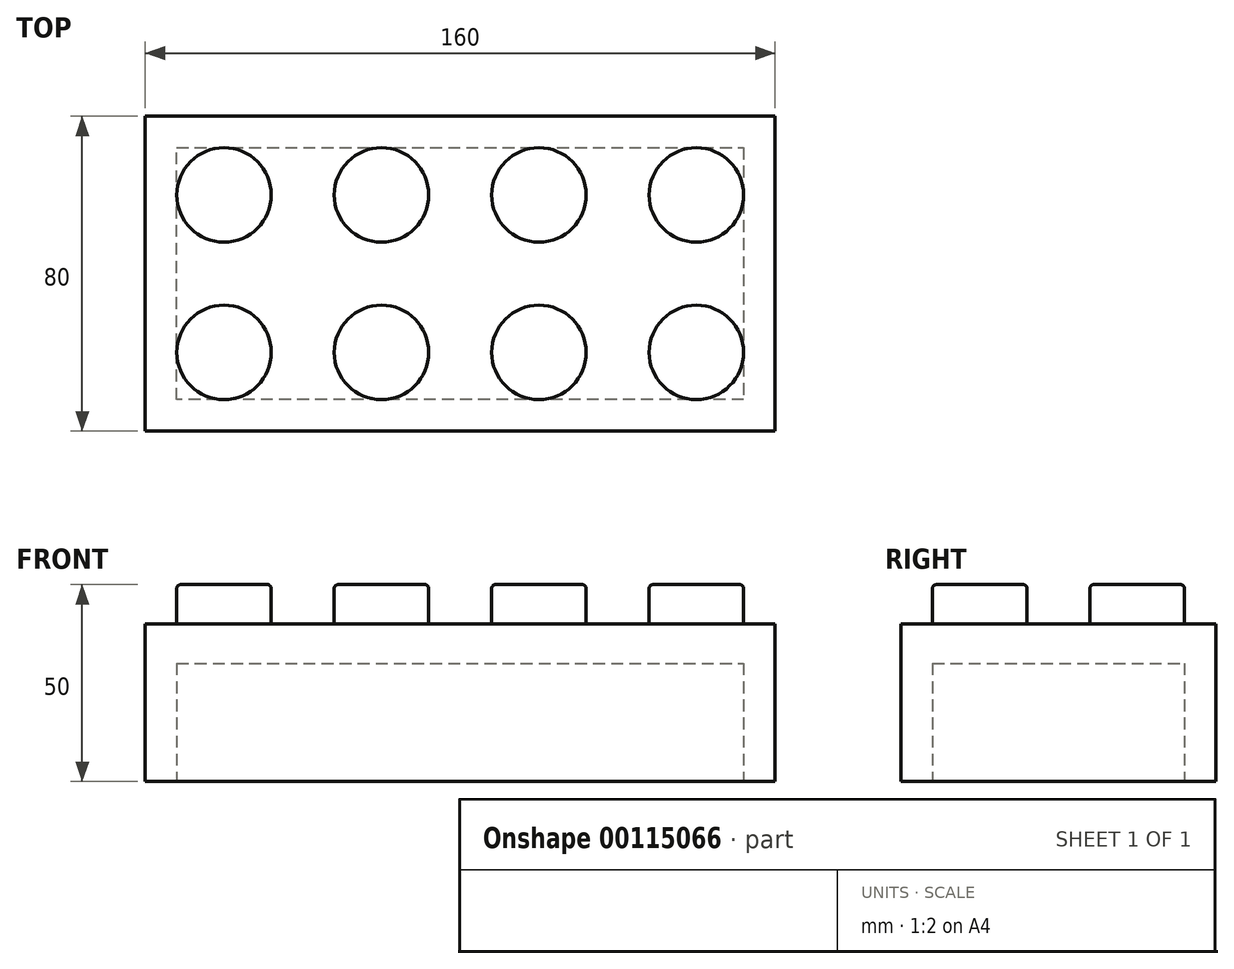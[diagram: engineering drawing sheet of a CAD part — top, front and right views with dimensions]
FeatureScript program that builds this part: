
annotation { "Feature Type Name" : "Feature", "Feature Type Description" : "" }
export const myFeature = defineFeature(function(context is Context, id is Id, definition is map)
    precondition{}
    {
        {
            var Q0;
            Q0=qCreatedBy(makeId("Top.planeOp"),FACE);
            var sketch = newSketch(context, id + "F0", { "sketchPlane" : qUnion([Q0])});
            skLineSegment(sketch, "E0.bottom", {"start": v(-96.29, 42.55) * mm, "end": v(63.71, 42.55) * mm});
            skLineSegment(sketch, "E0.top", {"start": v(-96.29, -37.45) * mm, "end": v(63.71, -37.45) * mm});
            skLineSegment(sketch, "E0.left", {"start": v(-96.29, 42.55) * mm, "end": v(-96.29, -37.45) * mm});
            skLineSegment(sketch, "E0.right", {"start": v(63.71, 42.55) * mm, "end": v(63.71, -37.45) * mm});
            skSolve(sketch);
        }
        {
            var Q0;
            Q0 = qSketchRegion(id + "F0", true);
            extrude(context, id + "F1", {"entities" : qUnion([Q0]), "depth" : 40 * mm});
        }
        {
            var Q0;
            Q0=makeQuery(id+"F1.opExtrude","CAP_FACE",FACE,{"disambiguationData":[OSD([sQuery(id+"F0.wireOp",EDGE,"E0.bottom"),sQuery(id+"F0.wireOp",EDGE,"E0.top"),sQuery(id+"F0.wireOp",EDGE,"E0.left"),sQuery(id+"F0.wireOp",EDGE,"E0.right")])],"isStart":true});
            var sketch = newSketch(context, id + "F2", { "sketchPlane" : qUnion([Q0])});
            skLineSegment(sketch, "E1.0", {"start": v(-88.29, -34.55) * mm, "end": v(55.71, -34.55) * mm});
            skLineSegment(sketch, "E1.1", {"start": v(-88.29, 29.45) * mm, "end": v(-88.29, -34.55) * mm});
            skLineSegment(sketch, "E1.2", {"start": v(55.71, 29.45) * mm, "end": v(-88.29, 29.45) * mm});
            skLineSegment(sketch, "E1.3", {"start": v(55.71, -34.55) * mm, "end": v(55.71, 29.45) * mm});
            skSolve(sketch);
        }
        {
            var Q0;
            Q0 = qSketchRegion(id + "F2", true);
            extrude(context, id + "F3", {"entities" : qUnion([Q0]), "operationType" : NewBodyOperationType.REMOVE, "oppositeDirection" : true, "depth" : 30 * mm});
        }
        {
            var Q0;
            Q0=makeQuery(id+"F1.opExtrude","CAP_FACE",FACE,{"disambiguationData":[OSD([sQuery(id+"F0.wireOp",EDGE,"E0.bottom"),sQuery(id+"F0.wireOp",EDGE,"E0.top"),sQuery(id+"F0.wireOp",EDGE,"E0.left"),sQuery(id+"F0.wireOp",EDGE,"E0.right")])],"isStart":false});
            var sketch = newSketch(context, id + "F4", { "sketchPlane" : qUnion([Q0])});
            skCircle(sketch, "E2", {"center": v(-76.29, 22.55) * mm, "radius": 12 * mm});
            skCircle(sketch, "E3.0.1.0", {"center": v(-76.29, -17.45) * mm, "radius": 12 * mm});
            skCircle(sketch, "E3.1.0.0", {"center": v(-36.29, 22.55) * mm, "radius": 12 * mm});
            skCircle(sketch, "E3.1.1.0", {"center": v(-36.29, -17.45) * mm, "radius": 12 * mm});
            skCircle(sketch, "E3.2.0.0", {"center": v(3.71, 22.55) * mm, "radius": 12 * mm});
            skCircle(sketch, "E3.2.1.0", {"center": v(3.71, -17.45) * mm, "radius": 12 * mm});
            skCircle(sketch, "E3.3.0.0", {"center": v(43.71, 22.55) * mm, "radius": 12 * mm});
            skCircle(sketch, "E3.3.1.0", {"center": v(43.71, -17.45) * mm, "radius": 12 * mm});
            skLineSegment(sketch, "E3.direction1", {"start": v(-76.29, 22.55) * mm, "end": v(-36.29, 22.55) * mm, "construction": true});
            skLineSegment(sketch, "E3.direction2", {"start": v(-76.29, 22.55) * mm, "end": v(-76.29, -17.45) * mm, "construction": true});
            skSolve(sketch);
        }
        {
            var Q0;
            Q0 = qSketchRegion(id + "F4", true);
            extrude(context, id + "F5", {"entities" : qUnion([Q0]), "operationType" : NewBodyOperationType.ADD, "depth" : 10 * mm});
        }
        {
            var Q0;
            Q0=makeQuery(id+"F5.opExtrude","CAP_FACE",FACE,{"disambiguationData":[OSD([sQuery(id+"F4.wireOp",EDGE,"E2")])],"isStart":false});
            var Q1;
            Q1=makeQuery(id+"F5.opExtrude","CAP_FACE",FACE,{"disambiguationData":[OSD([sQuery(id+"F4.wireOp",EDGE,"E3.1.0.0")])],"isStart":false});
            var Q2;
            Q2=makeQuery(id+"F5.opExtrude","CAP_FACE",FACE,{"disambiguationData":[OSD([sQuery(id+"F4.wireOp",EDGE,"E3.2.0.0")])],"isStart":false});
            var Q3;
            Q3=makeQuery(id+"F5.opExtrude","CAP_FACE",FACE,{"disambiguationData":[OSD([sQuery(id+"F4.wireOp",EDGE,"E3.3.0.0")])],"isStart":false});
            var Q4;
            Q4=makeQuery(id+"F5.opExtrude","CAP_FACE",FACE,{"disambiguationData":[OSD([sQuery(id+"F4.wireOp",EDGE,"E3.3.1.0")])],"isStart":false});
            var Q5;
            Q5=makeQuery(id+"F5.opExtrude","CAP_FACE",FACE,{"disambiguationData":[OSD([sQuery(id+"F4.wireOp",EDGE,"E3.2.1.0")])],"isStart":false});
            var Q6;
            Q6=makeQuery(id+"F5.opExtrude","CAP_FACE",FACE,{"disambiguationData":[OSD([sQuery(id+"F4.wireOp",EDGE,"E3.1.1.0")])],"isStart":false});
            var Q7;
            Q7=makeQuery(id+"F5.opExtrude","CAP_FACE",FACE,{"disambiguationData":[OSD([sQuery(id+"F4.wireOp",EDGE,"E3.0.1.0")])],"isStart":false});
            fillet(context, id + "F6", {"entities" : qUnion([Q0, Q1, Q2, Q3, Q4, Q5, Q6, Q7]), "radius" : 1 * mm, "tangentPropagation" : true, "allowEdgeOverflow" : false});
        }
    });
